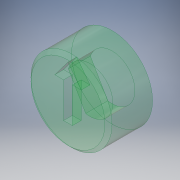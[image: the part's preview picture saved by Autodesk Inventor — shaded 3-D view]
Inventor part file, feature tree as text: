
AUTODESK INVENTOR PART (.ipt)
format: ipt  version: 2017 SP1 (Build 210196100, 196)  size: 148,992 bytes
history: native  units: in
note: dims shown in document units (in); Inventor stores cm internally (conversion verified against a paired STEP export)
features: extrude x5, sketch x5, chamfer x1, projected_geometry x1
ambient origin geometry x8: Origin, YZ Plane, XZ Plane, XY Plane, X Axis, Y Axis, Z Axis, Center Point
bodies: Solid1 (feature_tree)
feature tree (12):
  extrude  "Extrusion1"  Depth=0.0125in
  extrude  "Extrusion2"  Depth=1.0in
  extrude  "Extrusion3"  Depth=0.2in
  chamfer  "Chamfer1"  Distance=0.15in
  extrude  "Extrusion6"  Depth=0.05in TaperAngle=0.0deg
  extrude  "Extrusion7"  Depth=0.125in TaperAngle=45.0deg
  sketch  "Sketch1"  dims[d0=0.235in d2=0.0125in]
  sketch  "Sketch2"  dims[d3=1.0in d4=0.0in d5=0.1in]
  sketch  "Sketch3"  dims[d6=0.125in d7=0.0in d8=0.2in]
  sketch  "Sketch6"  dims[d9=0.1in]
  projected_geometry  "Projected Loop4"
  sketch  "Sketch7"  dims[d10=0.05in d11=0.15in d12=0.05in d13=0.0in d20=0.02in d21=0.125in d22=45.0deg d24=60.0deg d26=0.215in d27=0.4in d28=0.0in d29=0.25in d30=0.0in]
